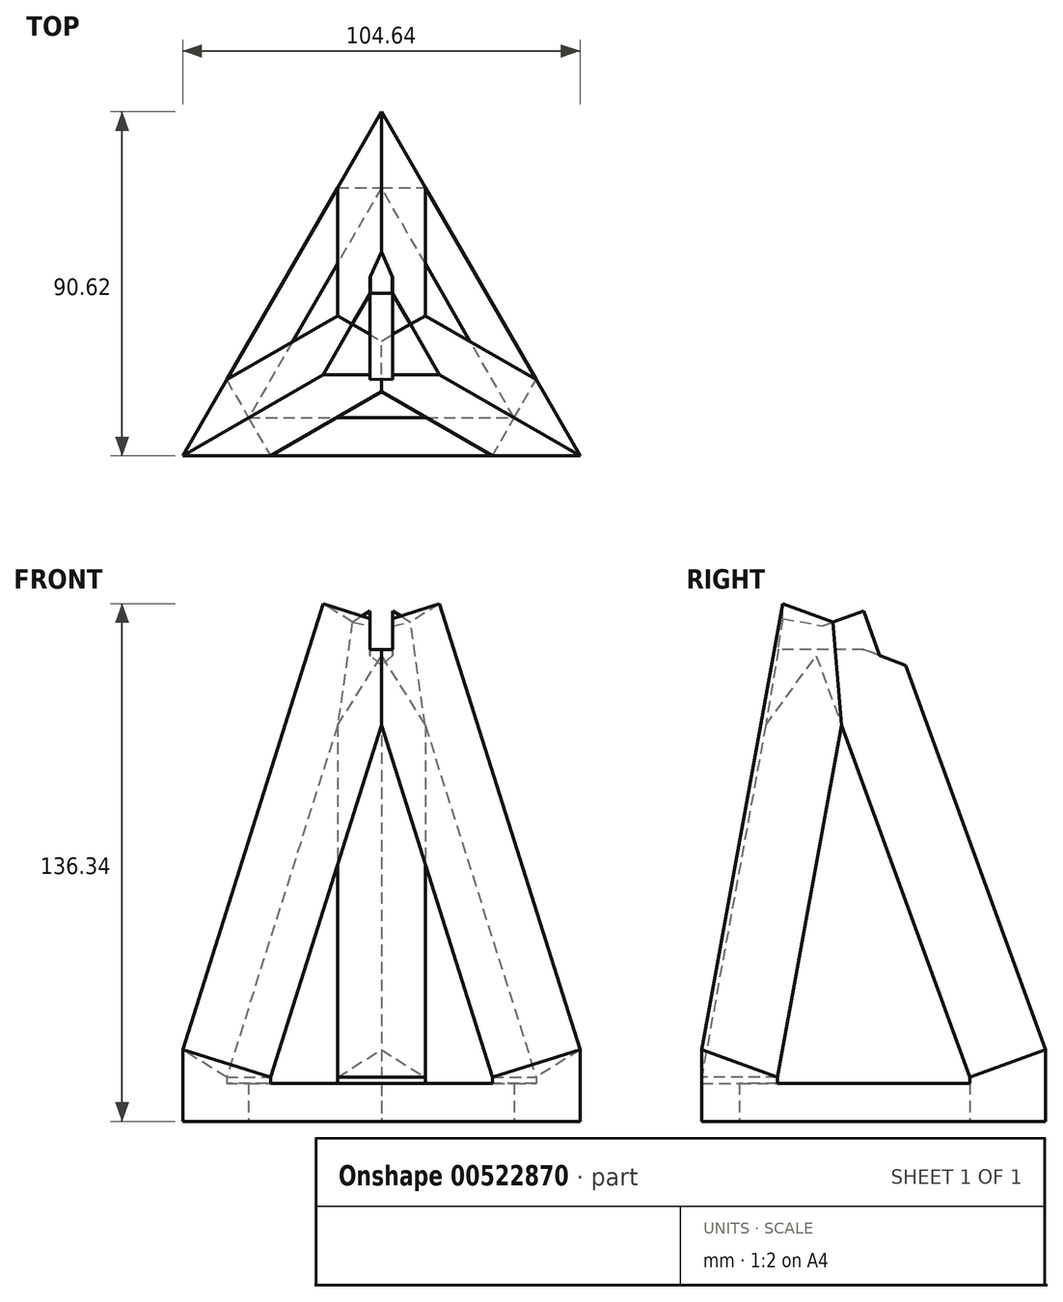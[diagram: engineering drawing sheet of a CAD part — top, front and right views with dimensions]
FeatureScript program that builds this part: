
annotation { "Feature Type Name" : "Feature", "Feature Type Description" : "" }
export const myFeature = defineFeature(function(context is Context, id is Id, definition is map)
    precondition{}
    {
        {
            var Q0;
            Q0=qCreatedBy(makeId("Top.planeOp"),FACE);
            var sketch = newSketch(context, id + "F0", { "sketchPlane" : qUnion([Q0])});
            skLineSegment(sketch, "E0", {"start": v(0, 30.7) * mm, "end": v(-35, -29.92) * mm});
            skLineSegment(sketch, "E1", {"start": v(-35, -29.92) * mm, "end": v(35, -29.92) * mm});
            skLineSegment(sketch, "E2", {"start": v(35, -29.92) * mm, "end": v(0, 30.7) * mm});
            skLineSegment(sketch, "E3.0", {"start": v(0, 50.7) * mm, "end": v(-52.32, -39.92) * mm});
            skLineSegment(sketch, "E3.1", {"start": v(52.32, -39.92) * mm, "end": v(0, 50.7) * mm});
            skLineSegment(sketch, "E3.2", {"start": v(-52.32, -39.92) * mm, "end": v(52.32, -39.92) * mm});
            skSolve(sketch);
        }
        {
            var Q0;
            Q0=makeQuery(id+"F0.imprint","IMPRINT",FACE,{"disambiguationData":[TD([[makeQuery(id+"F0.imprint","IMPRINT",EDGE,{"derivedFrom":sQuery(id+"F0.wireOp",EDGE,"E0")}),-1.0]])]});
            extrude(context, id + "F1", {"entities" : qUnion([Q0]), "depth" : 10 * mm, "offsetDistance" : 25 * mm});
        }
        {
            var Q0;
            Q0=makeQuery(id+"F1.opExtrude","CAP_FACE",FACE,{"disambiguationData":[OSD([sQuery(id+"F0.wireOp",EDGE,"E0"),sQuery(id+"F0.wireOp",EDGE,"E1"),sQuery(id+"F0.wireOp",EDGE,"E2"),sQuery(id+"F0.wireOp",EDGE,"E3.0"),sQuery(id+"F0.wireOp",EDGE,"E3.1"),sQuery(id+"F0.wireOp",EDGE,"E3.2")])],"isStart":false});
            var sketch = newSketch(context, id + "F2", { "sketchPlane" : qUnion([Q0])});
            skLineSegment(sketch, "E4", {"start": v(0, 50.7) * mm, "end": v(-11.55, 30.7) * mm});
            skLineSegment(sketch, "E5", {"start": v(-11.55, 30.7) * mm, "end": v(11.55, 30.7) * mm});
            skLineSegment(sketch, "E6", {"start": v(11.55, 30.7) * mm, "end": v(0, 50.7) * mm});
            skLineSegment(sketch, "E7", {"start": v(-52.32, -39.92) * mm, "end": v(-40.77, -19.92) * mm});
            skLineSegment(sketch, "E8", {"start": v(-40.77, -19.92) * mm, "end": v(-29.23, -39.92) * mm});
            skLineSegment(sketch, "E9", {"start": v(-29.23, -39.92) * mm, "end": v(-52.32, -39.92) * mm});
            skLineSegment(sketch, "E10", {"start": v(52.32, -39.92) * mm, "end": v(29.23, -39.92) * mm});
            skLineSegment(sketch, "E11", {"start": v(29.23, -39.92) * mm, "end": v(40.77, -19.92) * mm});
            skLineSegment(sketch, "E12", {"start": v(40.77, -19.92) * mm, "end": v(52.32, -39.92) * mm});
            skSolve(sketch);
        }
        {
            var Q0;
            {var subQ0=sQuery(id+"F2.wireOp",EDGE,"E4");Q0=makeQuery(id+"F2.imprint","IMPRINT",FACE,{"disambiguationData":[TD([[makeQuery(id+"F2.imprint","IMPRINT",EDGE,{"derivedFrom":subQ0}),1.0]])]});}
            var Q1;
            {var subQ0=sQuery(id+"F2.wireOp",EDGE,"E7");Q1=makeQuery(id+"F2.imprint","IMPRINT",FACE,{"disambiguationData":[TD([[makeQuery(id+"F2.imprint","IMPRINT",EDGE,{"derivedFrom":subQ0}),1.0]])]});}
            var Q2;
            {var subQ0=sQuery(id+"F2.wireOp",EDGE,"E10");Q2=makeQuery(id+"F2.imprint","IMPRINT",FACE,{"disambiguationData":[TD([[makeQuery(id+"F2.imprint","IMPRINT",EDGE,{"derivedFrom":subQ0}),1.0]])]});}
            extrude(context, id + "F3", {"entities" : qUnion([Q0, Q1, Q2]), "operationType" : NewBodyOperationType.ADD, "depth" : 10 * mm, "offsetDistance" : 25 * mm});
        }
        {
            var Q0;
            Q0=makeQuery(id+"F3.opExtrude","CAP_EDGE",EDGE,{"disambiguationData":[OSD([sQuery(id+"F2.wireOp",EDGE,"E5")])],"isStart":false});
            chamfer(context, id + "F4", {"entities" : qUnion([Q0]), "chamferType" : ChamferType.OFFSET_ANGLE, "width" : 23.1 * mm, "oppositeDirection" : false, "angle" : 20 * degree, "tangentPropagation" : true});
        }
        {
            var Q0;
            Q0=makeQuery(id+"F3.opExtrude","CAP_EDGE",EDGE,{"disambiguationData":[OSD([sQuery(id+"F2.wireOp",EDGE,"E8")])],"isStart":false});
            chamfer(context, id + "F5", {"entities" : qUnion([Q0]), "chamferType" : ChamferType.OFFSET_ANGLE, "width" : 23.1 * mm, "oppositeDirection" : true, "angle" : 20 * degree, "tangentPropagation" : true});
        }
        {
            var Q0;
            Q0=makeQuery(id+"F3.opExtrude","CAP_EDGE",EDGE,{"disambiguationData":[OSD([sQuery(id+"F2.wireOp",EDGE,"E11")])],"isStart":false});
            chamfer(context, id + "F6", {"entities" : qUnion([Q0]), "chamferType" : ChamferType.OFFSET_ANGLE, "width" : 23.1 * mm, "oppositeDirection" : true, "angle" : 20 * degree, "tangentPropagation" : true});
        }
        {
            var Q0;
            Q0=makeQuery(id+"F4.opChamfer","BLEND_FACE",FACE,{"disambiguationData":[OSD([sQuery(id+"F2.wireOp",EDGE,"E5")])]});
            extrude(context, id + "F7", {"entities" : qUnion([Q0]), "operationType" : NewBodyOperationType.ADD, "depth" : 125 * mm, "offsetDistance" : 25 * mm});
        }
        {
            var Q0;
            Q0=makeQuery(id+"F5.opChamfer","BLEND_FACE",FACE,{"disambiguationData":[OSD([sQuery(id+"F2.wireOp",EDGE,"E8")])]});
            extrude(context, id + "F8", {"entities" : qUnion([Q0]), "operationType" : NewBodyOperationType.ADD, "depth" : 125 * mm, "offsetDistance" : 25 * mm});
        }
        {
            var Q0;
            Q0=makeQuery(id+"F6.opChamfer","BLEND_FACE",FACE,{"disambiguationData":[OSD([sQuery(id+"F2.wireOp",EDGE,"E11")])]});
            extrude(context, id + "F9", {"entities" : qUnion([Q0]), "operationType" : NewBodyOperationType.ADD, "depth" : 125 * mm, "offsetDistance" : 25 * mm});
        }
        {
            var Q0;
            Q0=makeQuery(id+"F7.opExtrude","CAP_VERTEX",VERTEX,{"disambiguationData":[OSD([sQuery(id+"F0.wireOp",EDGE,"E3.0"),sQuery(id+"F0.wireOp",EDGE,"E3.1"),sQuery(id+"F2.wireOp",EDGE,"E4"),sQuery(id+"F2.wireOp",EDGE,"E5"),sQuery(id+"F2.wireOp",EDGE,"E6"),sQuery(id+"F2.wireOp",EDGE,"E7"),sQuery(id+"F2.wireOp",EDGE,"E12")])],"isStart":false});
            var Q1;
            Q1=makeQuery(id+"F9.opExtrude","CAP_VERTEX",VERTEX,{"disambiguationData":[OSD([sQuery(id+"F0.wireOp",EDGE,"E3.1"),sQuery(id+"F0.wireOp",EDGE,"E3.2"),sQuery(id+"F2.wireOp",EDGE,"E6"),sQuery(id+"F2.wireOp",EDGE,"E9"),sQuery(id+"F2.wireOp",EDGE,"E10"),sQuery(id+"F2.wireOp",EDGE,"E11"),sQuery(id+"F2.wireOp",EDGE,"E12")])],"isStart":false});
            var Q2;
            Q2=makeQuery(id+"F8.opExtrude","CAP_VERTEX",VERTEX,{"disambiguationData":[OSD([sQuery(id+"F0.wireOp",EDGE,"E3.0"),sQuery(id+"F0.wireOp",EDGE,"E3.2"),sQuery(id+"F2.wireOp",EDGE,"E4"),sQuery(id+"F2.wireOp",EDGE,"E7"),sQuery(id+"F2.wireOp",EDGE,"E8"),sQuery(id+"F2.wireOp",EDGE,"E9"),sQuery(id+"F2.wireOp",EDGE,"E10")])],"isStart":false});
            cPlane(context, id + "F10", {"entities" : qUnion([Q0, Q1, Q2]), "cplaneType" : CPlaneType.THREE_POINT, "offset" : 25 * mm, "width" : 150 * mm, "height" : 150 * mm});
        }
        {
            var Q0;
            Q0=qCreatedBy(id+"F10.planeOp",FACE);
            var sketch = newSketch(context, id + "F11", { "sketchPlane" : qUnion([Q0])});
            skLineSegment(sketch, "E13.bottom", {"start": v(-3, 40.28) * mm, "end": v(3, 40.28) * mm});
            skLineSegment(sketch, "E13.top", {"start": v(-3, -59.72) * mm, "end": v(3, -59.72) * mm});
            skLineSegment(sketch, "E13.left", {"start": v(-3, 40.28) * mm, "end": v(-3, -59.72) * mm});
            skLineSegment(sketch, "E13.right", {"start": v(3, 40.28) * mm, "end": v(3, -59.72) * mm});
            skPoint(sketch, "E13.middle", {"position": v(0, -9.72) * mm});
            skSolve(sketch);
        }
        {
            var Q0;
            Q0 = qSketchRegion(id + "F11", true);
            extrude(context, id + "F12", {"entities" : qUnion([Q0]), "operationType" : NewBodyOperationType.REMOVE, "oppositeDirection" : true, "depth" : 12 * mm, "offsetDistance" : 25 * mm});
        }
        {
            var Q0;
            Q0=makeQuery(id+"F12.boolean.opBoolean","INTERSECT",EDGE,{"derivedFrom":[makeQuery(id+"F7.opExtrude","SWEPT_FACE",FACE,{"disambiguationData":[OSD([sQuery(id+"F0.wireOp",EDGE,"E3.1"),sQuery(id+"F2.wireOp",EDGE,"E5"),sQuery(id+"F2.wireOp",EDGE,"E6"),sQuery(id+"F2.wireOp",EDGE,"E12")])]}),makeQuery(id+"F12.opExtrude","CAP_FACE",FACE,{"disambiguationData":[OSD([sQuery(id+"F11.wireOp",EDGE,"E13.bottom"),sQuery(id+"F11.wireOp",EDGE,"E13.top"),sQuery(id+"F11.wireOp",EDGE,"E13.left"),sQuery(id+"F11.wireOp",EDGE,"E13.right")])],"isStart":false})]});
            var Q1;
            Q1=makeQuery(id+"F12.boolean.opBoolean","INTERSECT",EDGE,{"derivedFrom":[makeQuery(id+"F7.opExtrude","SWEPT_FACE",FACE,{"disambiguationData":[OSD([sQuery(id+"F0.wireOp",EDGE,"E3.0"),sQuery(id+"F2.wireOp",EDGE,"E4"),sQuery(id+"F2.wireOp",EDGE,"E5"),sQuery(id+"F2.wireOp",EDGE,"E7")])]}),makeQuery(id+"F12.opExtrude","CAP_FACE",FACE,{"disambiguationData":[OSD([sQuery(id+"F11.wireOp",EDGE,"E13.bottom"),sQuery(id+"F11.wireOp",EDGE,"E13.top"),sQuery(id+"F11.wireOp",EDGE,"E13.left"),sQuery(id+"F11.wireOp",EDGE,"E13.right")])],"isStart":false})]});
            chamfer(context, id + "F13", {"entities" : qUnion([Q0, Q1]), "width" : 2 * mm, "tangentPropagation" : true});
        }
        {
            var Q0;
            {var subQ0=makeQuery(id+"F12.opExtrude","CAP_FACE",FACE,{"disambiguationData":[OSD([sQuery(id+"F11.wireOp",EDGE,"E13.bottom"),sQuery(id+"F11.wireOp",EDGE,"E13.top"),sQuery(id+"F11.wireOp",EDGE,"E13.left"),sQuery(id+"F11.wireOp",EDGE,"E13.right")])],"isStart":false});var subQ1=sQuery(id+"F2.wireOp",EDGE,"E5");Q0=makeQuery(id+"F13.opChamfer","BLEND_EDGE",EDGE,{"blendedFrom":[makeQuery(id+"F12.boolean.opBoolean","INTERSECT",EDGE,{"derivedFrom":[makeQuery(id+"F7.opExtrude","SWEPT_FACE",FACE,{"disambiguationData":[OSD([sQuery(id+"F0.wireOp",EDGE,"E3.0"),sQuery(id+"F2.wireOp",EDGE,"E4"),subQ1,sQuery(id+"F2.wireOp",EDGE,"E7")])]}),subQ0]}),makeQuery(id+"F12.boolean.opBoolean","INTERSECT",EDGE,{"derivedFrom":[makeQuery(id+"F7.opExtrude","SWEPT_FACE",FACE,{"disambiguationData":[OSD([sQuery(id+"F0.wireOp",EDGE,"E3.1"),subQ1,sQuery(id+"F2.wireOp",EDGE,"E6"),sQuery(id+"F2.wireOp",EDGE,"E12")])]}),subQ0]})],"blendedInto":[]});}
            chamfer(context, id + "F14", {"entities" : qUnion([Q0]), "width" : 5 * mm, "tangentPropagation" : true});
        }
    });
